# Revit family: CADS_Vent-Axia_MechEquip_Fan_ESC_3Ph2P - SUPPLY
name_source: partatom
category: Mechanical Equipment
units: mm (PartAtom-declared; Revit-internal decimal feet)

## family parameters
Always vertical = Yes
Cut with Voids When Loaded = No
OmniClass Number = 23.75.00.00
OmniClass Title = Climate Control (HVAC)
Part Type = Normal
Room Calculation Point = No
Round Connector Dimension = Use Diameter
Shared = No
Work Plane-Based = No

## types (3) — shared parameters
AirflowRateRange = 0.0 L/s
AssemblyPlace = UNKNOWN
AssetType = FIXED
DurationUnit = Year
ExteriorInsulation = No
Fitting Type = Ignore
GrossWeight = 0.00 kg
HasProtectiveEarth = No
IfcExportAs = IfcFanType
IsExtendedWarranty = No
ManufacturerAddress = Fleming Way
Crawley 
RH10 9YX
Quantity = 1
RatedCurrent = 0 A
RatedVoltage = 0 V
Status = New
WarrantyGuarantor = Vent-Axia Limited
WorkingPressure = 0.0 Pa
zero-valued in all types: CADS_Index, CADS_Usage, Default Elevation, ExpectedServiceLife, NumberOfPoles

## per-type parameters (varying)
| type | ModelReference | NominalDiameter | NominalHeight | NominalLength | NominalWidth |
| ESC25032 | SHORT CASED AXIAL FAN 250DIA 3PH 2 POLE | 250 mm  [stored 0.82021 ft] | 250 mm  [stored 0.82021 ft] | 110 mm  [stored 0.360892 ft] | 250 mm  [stored 0.82021 ft] |
| ESC31532 | SHORT CASED AXIAL FAN 315DIA 3PH 2 POLE | 315 mm  [stored 1.03346 ft] | 315 mm  [stored 1.03346 ft] | 135 mm  [stored 0.442913 ft] | 315 mm  [stored 1.03346 ft] |
| ESC35532 | SHORT CASED AXIAL FAN 355DIA 3PH 2 POLE | 355 mm | 355 mm | 135 mm  [stored 0.442913 ft] | 355 mm |

note: column(s) folded — value = type name in every type: ModelNumber

note: [stored X ft] marks values corroborated as IEEE doubles in the binary element streams (Revit-internal decimal feet)

## geometry (parser evidence)
native form markers: Sweep x13
no freeform markers — native parametric forms only
